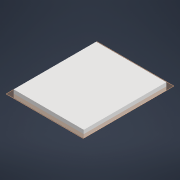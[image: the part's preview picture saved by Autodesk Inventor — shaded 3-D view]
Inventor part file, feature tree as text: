
AUTODESK INVENTOR PART (.ipt)
format: ipt  version: 2022 (Build 260153000, 153)  size: 87,552 bytes
history: native  units: mm
features: other x2, extrude x1, sketch x1
ambient origin geometry x8: Origin, YZ Plane, XZ Plane, XY Plane, X Axis, Y Axis, Z Axis, Center Point
bodies: Body1 (feature_tree)
feature tree (4):
  other  "Твердое тело1"
  extrude  "Выдавливание1"  Depth=209.0mm
  other  "РабПлоскость1"
  sketch  "Эскиз1"
